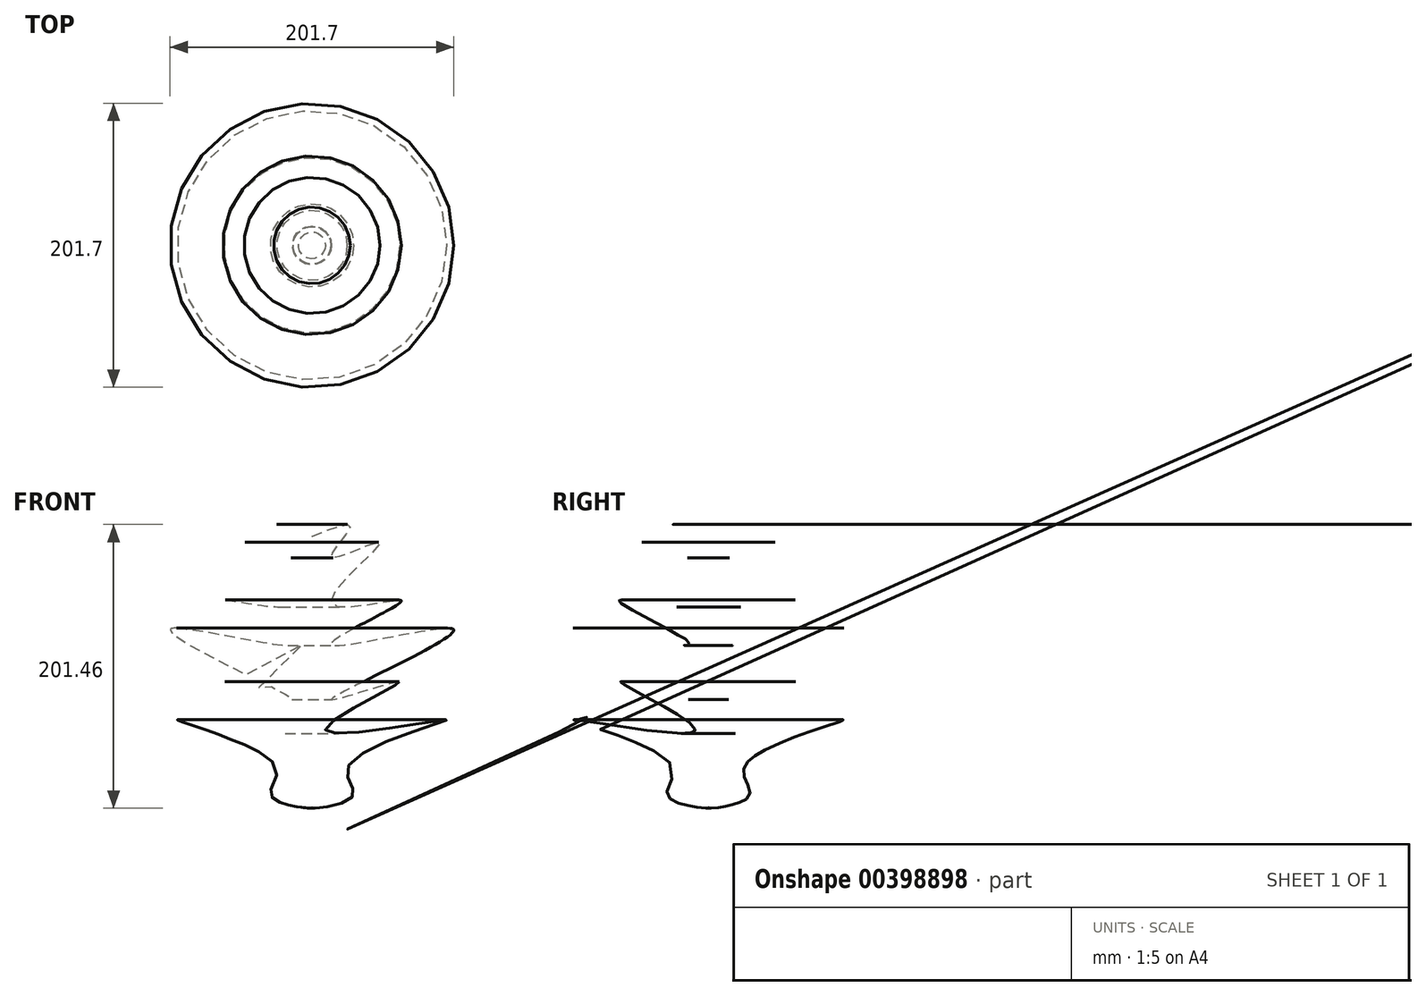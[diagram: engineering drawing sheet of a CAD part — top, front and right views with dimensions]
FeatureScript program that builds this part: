
annotation { "Feature Type Name" : "Feature", "Feature Type Description" : "" }
export const myFeature = defineFeature(function(context is Context, id is Id, definition is map)
    precondition{}
    {
        {
            var Q0;
            Q0=qCreatedBy(makeId("Front.planeOp"),FACE);
            var sketch = newSketch(context, id + "F0", { "sketchPlane" : qUnion([Q0])});
            skLineSegment(sketch, "E0", {"start": v(-13.75, 71.11) * mm, "end": v(-13.75, -121.75) * mm});
            skFitSpline(sketch, "E1", {"points": [v(-13.75, 71.11) * mm, v(13.4, 77.54) * mm, v(0, 56.1) * mm, v(34.54, 66.72) * mm, v(0, 23.56) * mm, v(49.7, 25.27) * mm, v(0, -5.54) * mm, v(87.07, 4.69) * mm, v(0, -44.77) * mm, v(48.64, -32.13) * mm, v(-4.23, -66.43) * mm, v(81.78, -59.23) * mm, v(12.69, -91.16) * mm, v(15.5, -112.9) * mm, v(-10.93, -121.94) * mm, v(-13.75, -121.75) * mm], "startDerivative": vector(826.52, 334.66) * mm, "endDerivative": vector(-93.79, 26.5) * mm});
            skSolve(sketch);
        }
        {
            var Q0;
            Q0=makeQuery(id+"F0.imprint","IMPRINT",FACE,{"disambiguationData":[TD([[makeQuery(id+"F0.imprint","IMPRINT",EDGE,{"derivedFrom":sQuery(id+"F0.wireOp",EDGE,"E0")}),1.0]])]});
            var Q1;
            Q1=sQuery(id+"F0.wireOp",EDGE,"E0");
            revolve(context, id + "F1", {"entities" : qUnion([Q0]), "axis" : qUnion([Q1]), "revolveType" : RevolveType.FULL});
        }
    });
